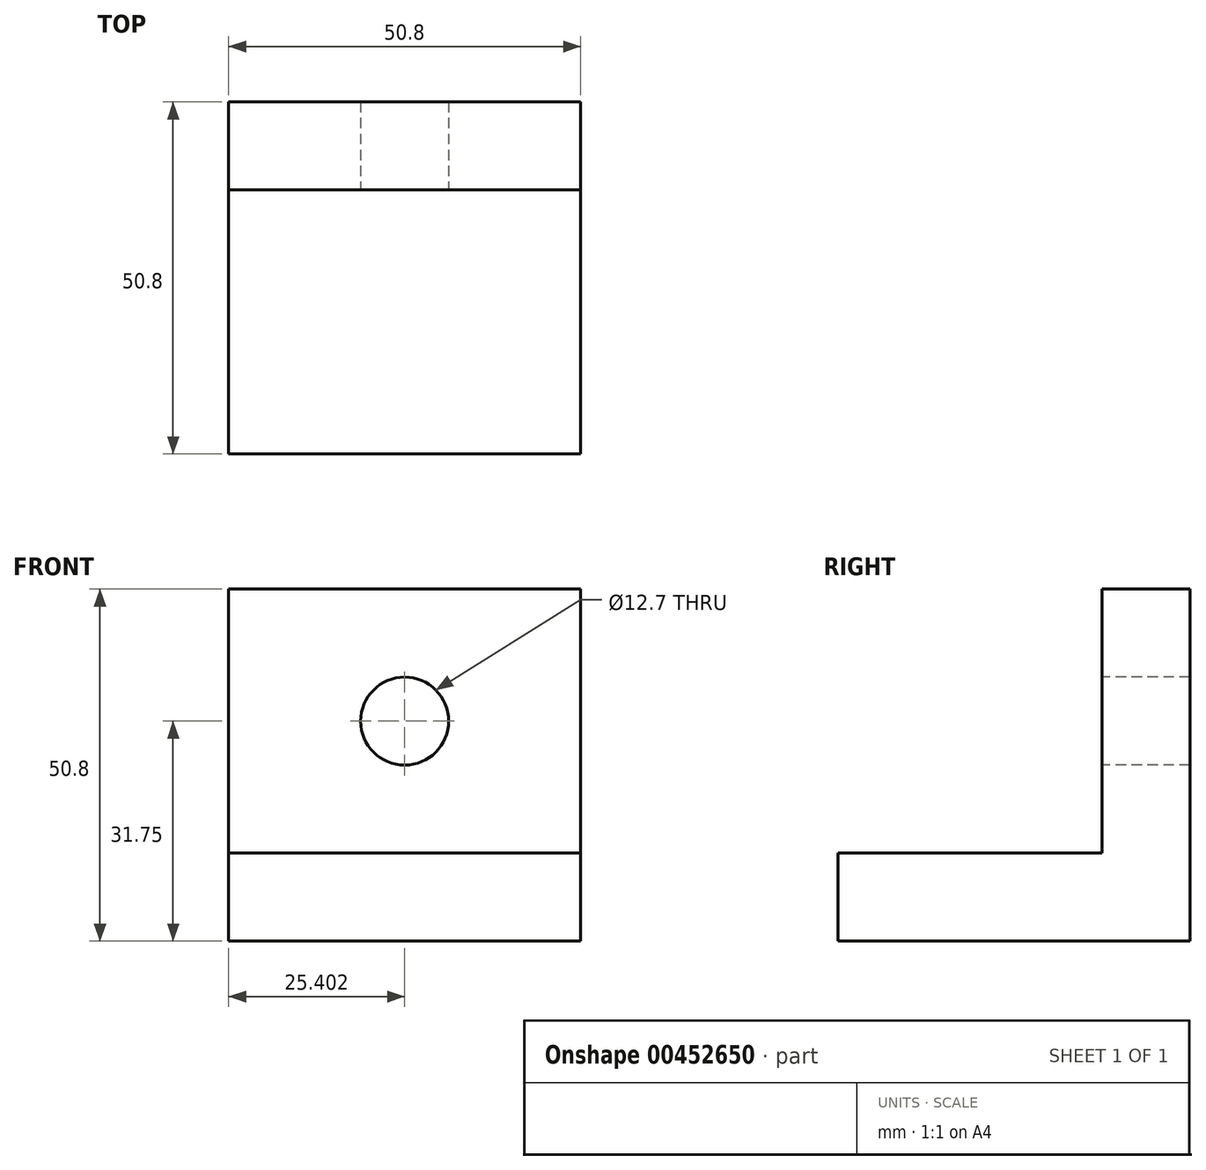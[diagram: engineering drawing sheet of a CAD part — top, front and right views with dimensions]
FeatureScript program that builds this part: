
annotation { "Feature Type Name" : "Feature", "Feature Type Description" : "" }
export const myFeature = defineFeature(function(context is Context, id is Id, definition is map)
    precondition{}
    {
        {
            var Q0;
            Q0=qCreatedBy(makeId("Top.planeOp"),FACE);
            var sketch = newSketch(context, id + "F0", { "sketchPlane" : qUnion([Q0])});
            skLineSegment(sketch, "E0.top", {"start": v(-17.5, -27.43) * mm, "end": v(33.3, -27.43) * mm});
            skLineSegment(sketch, "E0.left", {"start": v(-17.5, 23.37) * mm, "end": v(-17.5, -27.43) * mm});
            skLineSegment(sketch, "E0.right", {"start": v(33.3, 23.37) * mm, "end": v(33.3, -27.43) * mm});
            skLineSegment(sketch, "E1", {"start": v(-17.5, 23.37) * mm, "end": v(33.3, 23.37) * mm});
            skLineSegment(sketch, "E2", {"start": v(-17.5, 23.37) * mm, "end": v(-17.5, 10.67) * mm});
            skLineSegment(sketch, "E3", {"start": v(-17.5, 10.67) * mm, "end": v(33.3, 10.67) * mm});
            skLineSegment(sketch, "E4", {"start": v(33.3, 10.67) * mm, "end": v(33.3, 23.37) * mm});
            skSolve(sketch);
        }
        {
            var Q0;
            Q0=makeQuery(id+"F0.imprint","IMPRINT",FACE,{"disambiguationData":[TD([[makeQuery(id+"F0.imprint","IMPRINT",EDGE,{"derivedFrom":sQuery(id+"F0.wireOp",EDGE,"E1")}),-1.0]])]});
            extrude(context, id + "F1", {"entities" : qUnion([Q0]), "depth" : 50.8 * mm});
        }
        {
            var Q0;
            Q0 = qSketchRegion(id + "F0", true);
            extrude(context, id + "F2", {"entities" : qUnion([Q0]), "operationType" : NewBodyOperationType.ADD, "depth" : 12.7 * mm});
        }
        {
            var Q0;
            Q0=makeQuery(id+"F1.opExtrude","SWEPT_FACE",FACE,{"disambiguationData":[OSD([sQuery(id+"F0.wireOp",EDGE,"E3")])]});
            var sketch = newSketch(context, id + "F3", { "sketchPlane" : qUnion([Q0])});
            skCircle(sketch, "E5", {"center": v(7.9, 31.75) * mm, "radius": 6.35 * mm});
            skPoint(sketch, "E5.centerSnap0", {"position": v(33.3, 31.75) * mm});
            skPoint(sketch, "E5.centerSnap1", {"position": v(7.9, 50.8) * mm});
            skSolve(sketch);
        }
        {
            var Q0;
            Q0=makeQuery(id+"F3.imprint","IMPRINT",FACE,{"disambiguationData":[TD([[makeQuery(id+"F3.imprint","IMPRINT",EDGE,{"derivedFrom":sQuery(id+"F3.wireOp",EDGE,"E5")}),1.0]])]});
            extrude(context, id + "F4", {"entities" : qUnion([Q0]), "operationType" : NewBodyOperationType.REMOVE, "oppositeDirection" : true, "depth" : 25.4 * mm});
        }
    });
